# Revit family: Indoor_Floor Lamp_Santa&Cole_Fontana
name_source: partatom
category: Luminarias
revit_build: Autodesk Revit 2018 (Build: 20190510_1515(x64)
units: mm (PartAtom-declared; Revit-internal decimal feet)

## family parameters
Compartido = No
Corte con vacíos al cargar = No
Cota de conector redondo = Diámetro de uso
Número OmniClass = 23.80.70.00
Origen de luz = Sí
Punto de cálculo de habitación = No
Se basa en plano de trabajo = No
Siempre vertical = Sí
Tipo de pieza = Normal
Título OmniClass = Lighting

## types (1)
- Indoor_Floor Lamp_Santa&Cole_Fontana
    Archivo de red fotométrica = FOTSA01 (CL004A21F006G).IES
    Assembly instructions - CE = https://www.santacole.com
    Cambio de temperatura de color de luz atenuada = <Ninguno>
    Carga aparente = 40 VA
    Code = FOTSA01
    Fabricante = Santa & Cole
    Filtro de color = 16777215
    Lamp Material = <Por categoría>
    Load = 40 W
    Manufacturer website = http://www.santacole.com
    Modelo = Fontana Pie
    Technical Information = https://www.santacole.com
    URL = https://www.santacole.com
    Ángulo de inclinación = 90.00°

## geometry (parser evidence)
native form markers: Sweep x3
no freeform markers — native parametric forms only
